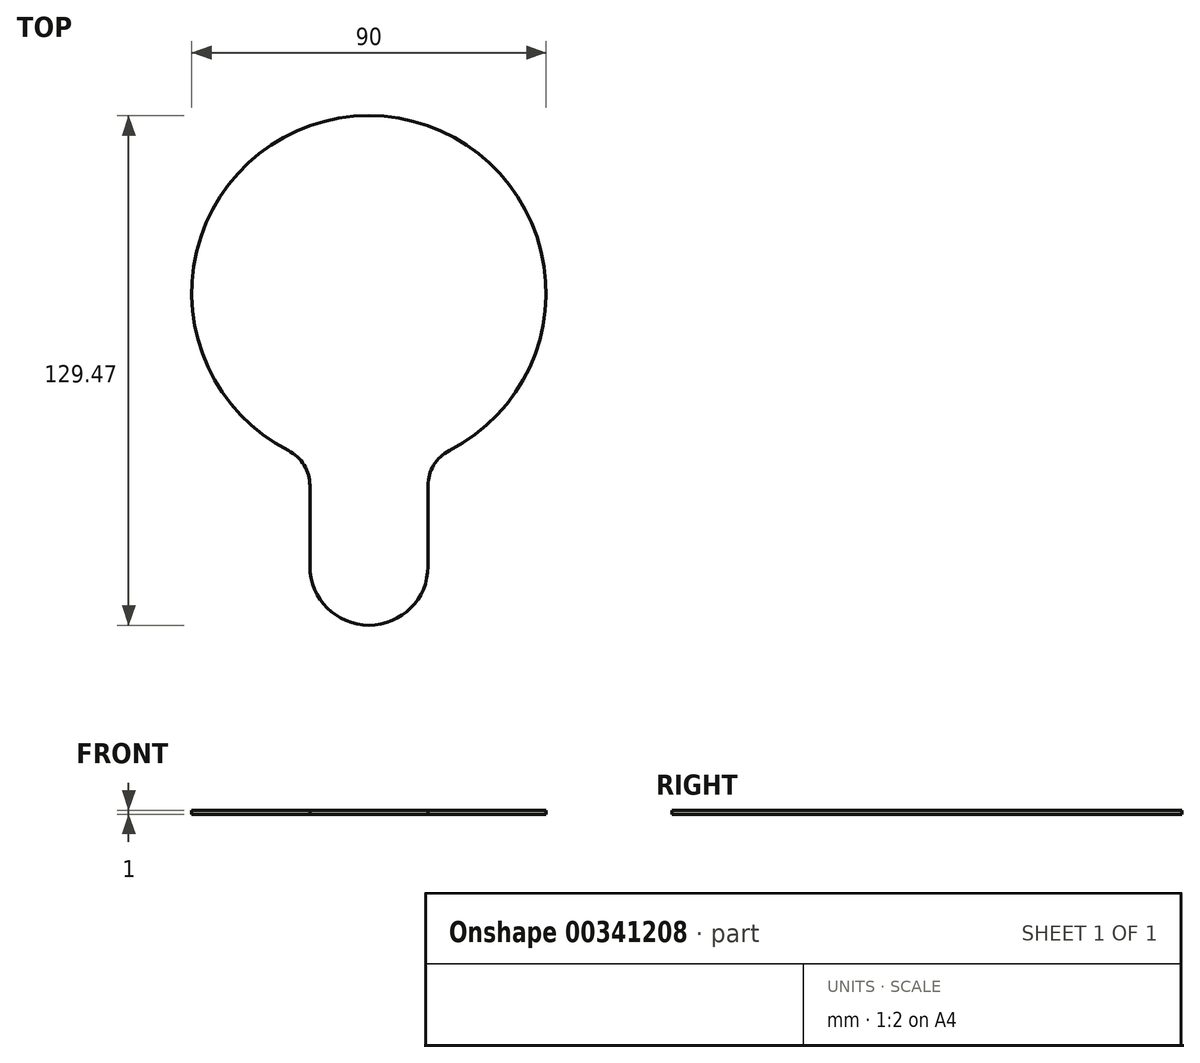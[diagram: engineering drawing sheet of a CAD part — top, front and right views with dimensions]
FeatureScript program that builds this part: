
annotation { "Feature Type Name" : "Feature", "Feature Type Description" : "" }
export const myFeature = defineFeature(function(context is Context, id is Id, definition is map)
    precondition{}
    {
        {
            var Q0;
            Q0=qCreatedBy(makeId("Top.planeOp"),FACE);
            var sketch = newSketch(context, id + "F0", { "sketchPlane" : qUnion([Q0])});
            skArc(sketch, "E0", {"start": v(20.45, -40.08) * mm, "mid": v(0, 45) * mm, "end": v(-20.45, -40.08) * mm});
            skLineSegment(sketch, "E1", {"start": v(-15, -48.99) * mm, "end": v(-15, -69.47) * mm});
            skLineSegment(sketch, "E2", {"start": v(15, -69.47) * mm, "end": v(15, -48.99) * mm});
            skArc(sketch, "E3", {"start": v(-15, -69.47) * mm, "mid": v(0, -84.47) * mm, "end": v(15, -69.47) * mm});
            skPoint(sketch, "E4.visualSharp", {"position": v(15, -42.43) * mm});
            skArc(sketch, "E4.filletArc", {"start": v(20.45, -40.08) * mm, "mid": v(16.47, -43.77) * mm, "end": v(15, -48.99) * mm});
            skPoint(sketch, "E5.visualSharp", {"position": v(-15, -42.43) * mm});
            skArc(sketch, "E5.filletArc", {"start": v(-15, -48.99) * mm, "mid": v(-16.47, -43.77) * mm, "end": v(-20.45, -40.08) * mm});
            skSolve(sketch);
        }
        {
            var Q0;
            Q0=makeQuery(id+"F0.imprint","IMPRINT",FACE,{"disambiguationData":[TD([[makeQuery(id+"F0.imprint","IMPRINT",EDGE,{"derivedFrom":sQuery(id+"F0.wireOp",EDGE,"E0")}),1.0]])]});
            extrude(context, id + "F1", {"entities" : qUnion([Q0]), "depth" : 1 * mm});
        }
    });
